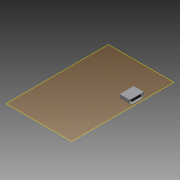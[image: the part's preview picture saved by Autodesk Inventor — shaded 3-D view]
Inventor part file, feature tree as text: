
AUTODESK INVENTOR PART (.ipt)
format: ipt  version: 2013 SP2 (Build 170200200, 200)  size: 105,984 bytes
history: native  units: mm
features: extrude x2, sketch x2, plane x1, chamfer x1, shell x1
ambient origin geometry x8: Origin, YZ Plane, XZ Plane, XY Plane, X Axis, Y Axis, Z Axis, Center Point
bodies: Solid1 (feature_tree)
feature tree (7):
  plane  "Work Plane2"
  extrude  "Extrusion1"  Depth=15.0mm
  chamfer  "Chamfer1"  Distance=5.6mm
  shell  "Shell1"  Thickness=0.3mm
  extrude  "Extrusion2"  Depth=1.0mm
  sketch  "Sketch1"  dims[d0=11.0mm d2=15.0mm d3=5.6mm d4=0.0mm]
  sketch  "Sketch2"  dims[d5=2.0mm d6=2.0mm d7=45.0deg d8=0.3mm d9=1.0mm d12=2.0mm d13=2.0mm d14=1.6mm d15=5.6mm d16=0.0mm]
